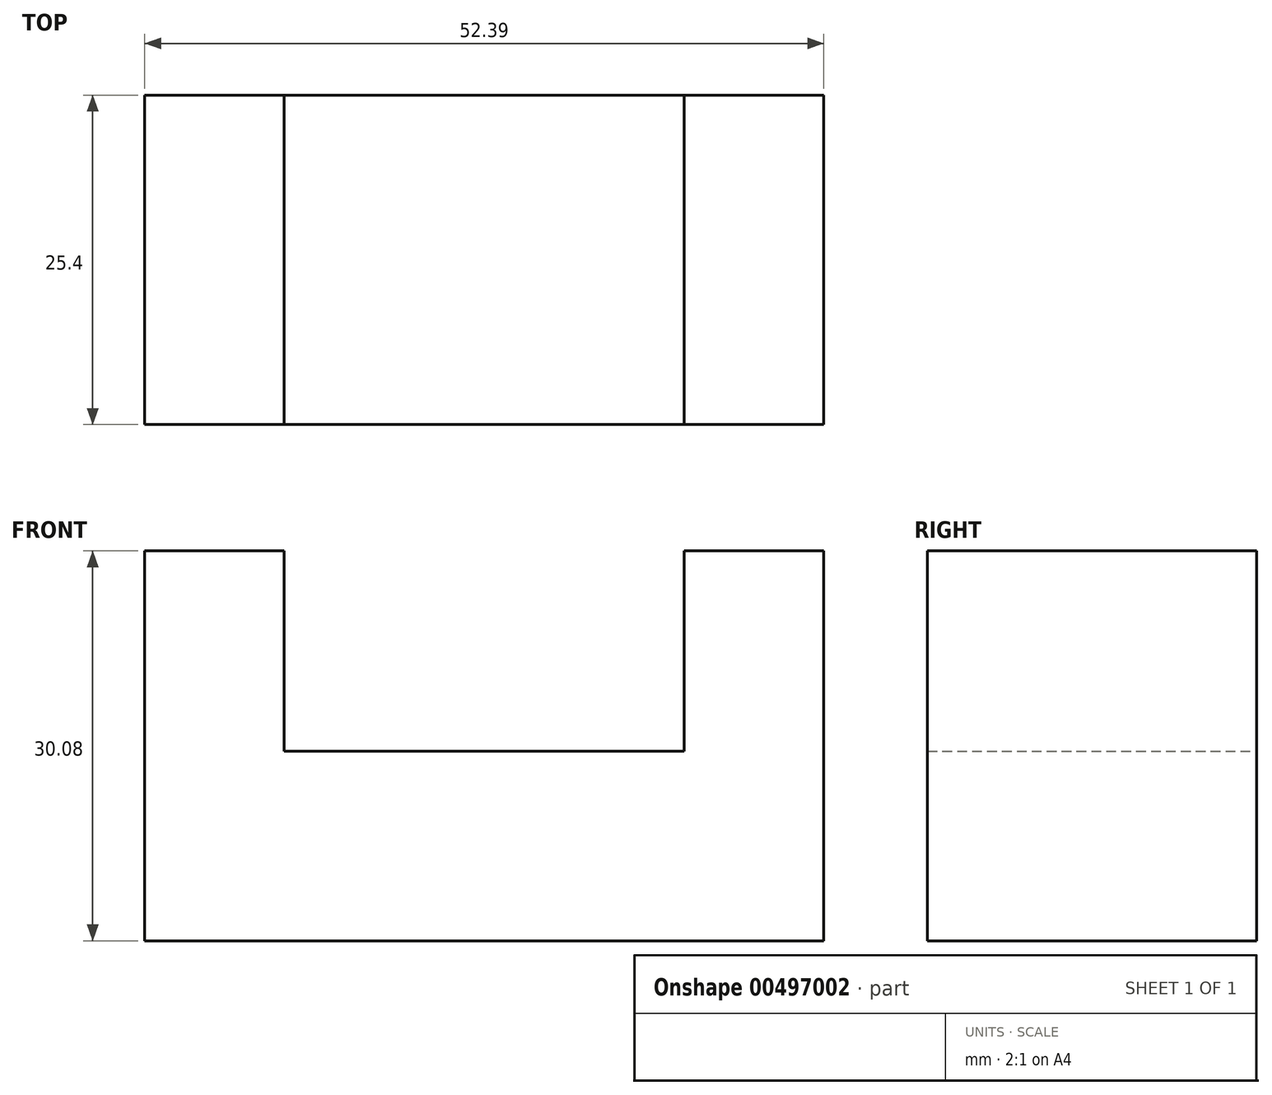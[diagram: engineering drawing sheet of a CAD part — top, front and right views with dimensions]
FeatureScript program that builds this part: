
annotation { "Feature Type Name" : "Feature", "Feature Type Description" : "" }
export const myFeature = defineFeature(function(context is Context, id is Id, definition is map)
    precondition{}
    {
        {
            var Q0;
            Q0=qCreatedBy(makeId("Front.planeOp"),FACE);
            var sketch = newSketch(context, id + "F0", { "sketchPlane" : qUnion([Q0])});
            skLineSegment(sketch, "E0.bottom", {"start": v(0, 0) * mm, "end": v(52.4, 0) * mm});
            skLineSegment(sketch, "E0.top", {"start": v(0, 30.08) * mm, "end": v(10.77, 30.08) * mm});
            skLineSegment(sketch, "E0.left", {"start": v(0, 0) * mm, "end": v(0, 30.08) * mm});
            skLineSegment(sketch, "E0.right", {"start": v(52.4, 0) * mm, "end": v(52.4, 30.08) * mm});
            skLineSegment(sketch, "E1.top", {"start": v(10.77, 14.63) * mm, "end": v(41.63, 14.63) * mm});
            skLineSegment(sketch, "E1.left", {"start": v(10.77, 30.08) * mm, "end": v(10.77, 14.63) * mm});
            skLineSegment(sketch, "E1.right", {"start": v(41.63, 30.08) * mm, "end": v(41.63, 14.63) * mm});
            skLineSegment(sketch, "E2.trimOffspring", {"start": v(41.63, 30.08) * mm, "end": v(52.4, 30.08) * mm});
            skSolve(sketch);
        }
        {
            var Q0;
            Q0=makeQuery(id+"F0.imprint","IMPRINT",FACE,{"disambiguationData":[TD([[makeQuery(id+"F0.imprint","IMPRINT",EDGE,{"derivedFrom":sQuery(id+"F0.wireOp",EDGE,"E0.bottom")}),1.0]])]});
            extrude(context, id + "F1", {"entities" : qUnion([Q0]), "depth" : 25.4 * mm});
        }
    });
